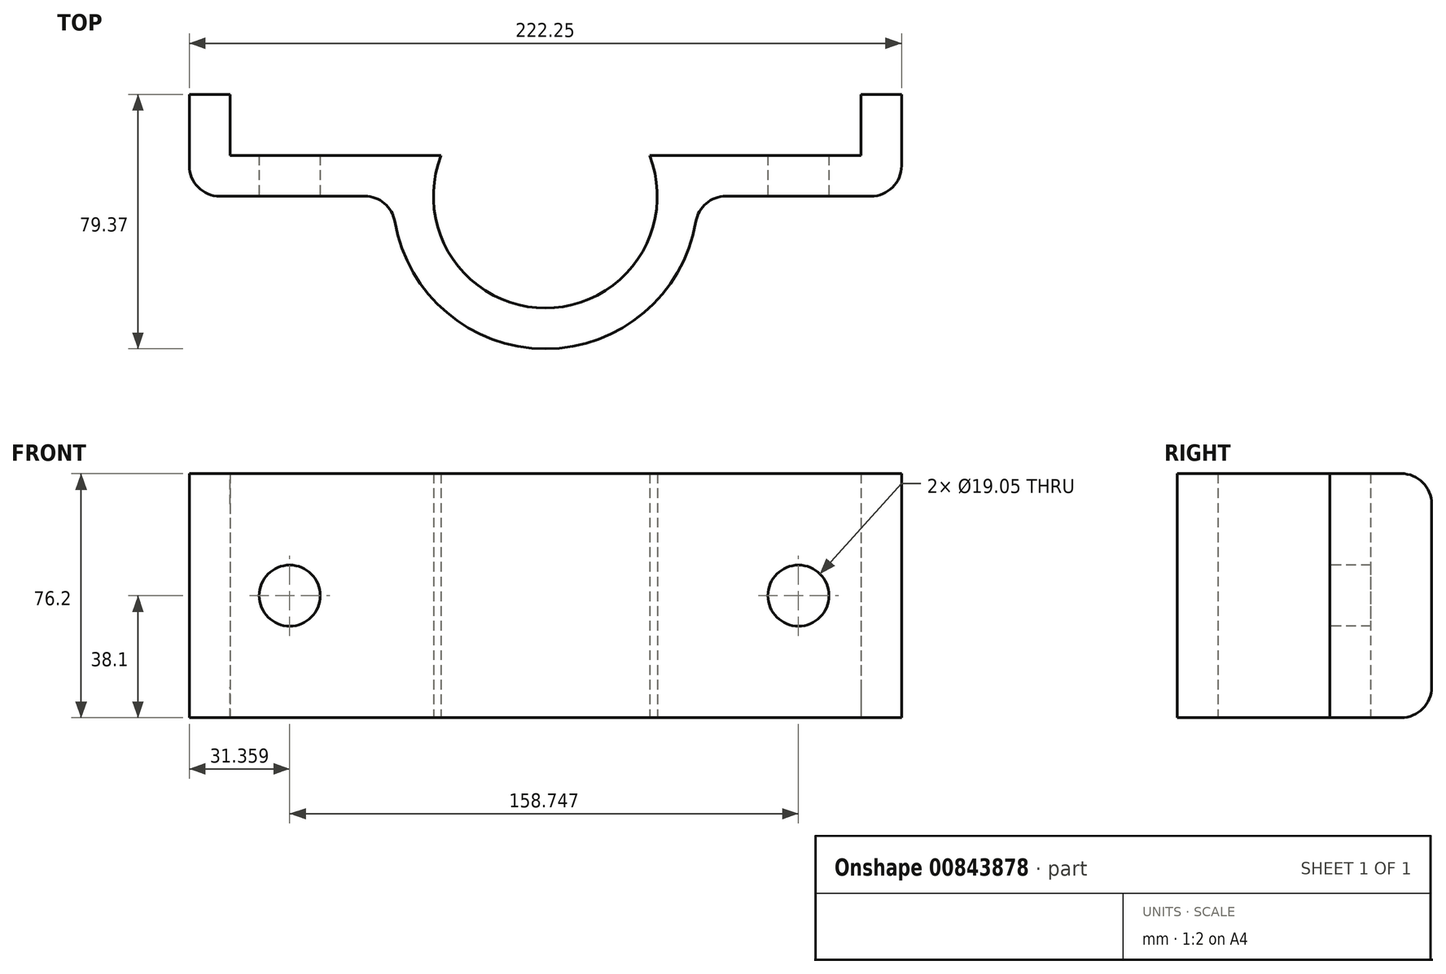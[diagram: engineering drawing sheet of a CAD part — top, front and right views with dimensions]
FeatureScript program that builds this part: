
annotation { "Feature Type Name" : "Feature", "Feature Type Description" : "" }
export const myFeature = defineFeature(function(context is Context, id is Id, definition is map)
    precondition{}
    {
        {
            var Q0;
            Q0=qCreatedBy(makeId("Top.planeOp"),FACE);
            var sketch = newSketch(context, id + "F0", { "sketchPlane" : qUnion([Q0])});
            skLineSegment(sketch, "E0", {"start": v(-41.29, 31.75) * mm, "end": v(-53.99, 31.75) * mm});
            skLineSegment(sketch, "E1", {"start": v(-53.99, 31.75) * mm, "end": v(-53.99, 9.52) * mm});
            skLineSegment(sketch, "E2", {"start": v(-41.29, 31.75) * mm, "end": v(-41.29, 12.7) * mm});
            skLineSegment(sketch, "E3", {"start": v(155.56, 31.75) * mm, "end": v(168.26, 31.75) * mm});
            skLineSegment(sketch, "E4", {"start": v(168.26, 31.75) * mm, "end": v(168.26, 9.53) * mm});
            skLineSegment(sketch, "E5", {"start": v(155.56, 12.7) * mm, "end": v(155.56, 31.75) * mm});
            skArc(sketch, "E6", {"start": v(24.6, 12.7) * mm, "mid": v(57.14, -34.93) * mm, "end": v(89.67, 12.7) * mm});
            skArc(sketch, "E7", {"start": v(10.18, -7.94) * mm, "mid": v(57.14, -47.62) * mm, "end": v(104.1, -7.94) * mm});
            skLineSegment(sketch, "E8", {"start": v(-41.29, 12.7) * mm, "end": v(24.6, 12.7) * mm});
            skLineSegment(sketch, "E9.trimOffspring", {"start": v(89.67, 12.7) * mm, "end": v(155.56, 12.7) * mm});
            skPoint(sketch, "E10.end.orphan", {"position": v(155.56, 0) * mm});
            skLineSegment(sketch, "E11", {"start": v(113.5, 0) * mm, "end": v(158.74, 0) * mm});
            skPoint(sketch, "E12.visualSharp", {"position": v(168.26, 0) * mm});
            skArc(sketch, "E12.filletArc", {"start": v(158.74, 0) * mm, "mid": v(165.47, 2.79) * mm, "end": v(168.26, 9.53) * mm});
            skPoint(sketch, "E13.visualSharp", {"position": v(104.76, 0) * mm});
            skArc(sketch, "E13.filletArc", {"start": v(113.5, 0) * mm, "mid": v(107.34, -2.25) * mm, "end": v(104.1, -7.94) * mm});
            skPoint(sketch, "E14.visualSharp", {"position": v(9.51, 0) * mm});
            skArc(sketch, "E14.filletArc", {"start": v(10.18, -7.94) * mm, "mid": v(6.94, -2.25) * mm, "end": v(0.79, 0) * mm});
            skPoint(sketch, "E15.end.orphan", {"position": v(-41.29, 0) * mm});
            skLineSegment(sketch, "E16", {"start": v(-44.46, 0) * mm, "end": v(0.79, 0) * mm});
            skPoint(sketch, "E17.visualSharp", {"position": v(-53.99, 0) * mm});
            skArc(sketch, "E17.filletArc", {"start": v(-53.99, 9.52) * mm, "mid": v(-51.2, 2.79) * mm, "end": v(-44.46, 0) * mm});
            skSolve(sketch);
        }
        {
            var Q0;
            Q0 = qSketchRegion(id + "F0", true);
            extrude(context, id + "F1", {"entities" : qUnion([Q0]), "depth" : 76.2 * mm, "offsetDistance" : 25.4 * mm});
        }
        {
            var Q0;
            Q0=makeQuery(id+"F1.opExtrude","SWEPT_FACE",FACE,{"disambiguationData":[OSD([sQuery(id+"F0.wireOp",EDGE,"E11")])]});
            var sketch = newSketch(context, id + "F2", { "sketchPlane" : qUnion([Q0])});
            skCircle(sketch, "E18", {"center": v(136.12, 38.1) * mm, "radius": 9.53 * mm});
            skPoint(sketch, "E19.orphan", {"position": v(136.12, 76.2) * mm});
            skPoint(sketch, "E20.start.orphan", {"position": v(136.12, 0) * mm});
            skCircle(sketch, "E21", {"center": v(-22.63, 38.1) * mm, "radius": 9.53 * mm});
            skSolve(sketch);
        }
        {
            var Q0;
            Q0 = qSketchRegion(id + "F2", true);
            extrude(context, id + "F3", {"entities" : qUnion([Q0]), "operationType" : NewBodyOperationType.REMOVE, "oppositeDirection" : true, "depth" : 25.4 * mm, "offsetDistance" : 25.4 * mm});
        }
        {
            var Q0;
            Q0=makeQuery(id+"F1.opExtrude","CAP_EDGE",EDGE,{"disambiguationData":[OSD([sQuery(id+"F0.wireOp",EDGE,"E0")])],"isStart":false});
            var Q1;
            Q1=makeQuery(id+"F1.opExtrude","CAP_EDGE",EDGE,{"disambiguationData":[OSD([sQuery(id+"F0.wireOp",EDGE,"E0")])],"isStart":true});
            var Q2;
            Q2=makeQuery(id+"F1.opExtrude","CAP_EDGE",EDGE,{"disambiguationData":[OSD([sQuery(id+"F0.wireOp",EDGE,"E3")])],"isStart":true});
            var Q3;
            Q3=makeQuery(id+"F1.opExtrude","CAP_EDGE",EDGE,{"disambiguationData":[OSD([sQuery(id+"F0.wireOp",EDGE,"E3")])],"isStart":false});
            fillet(context, id + "F4", {"entities" : qUnion([Q0, Q1, Q2, Q3]), "radius" : 9.52 * mm, "tangentPropagation" : true, "allowEdgeOverflow" : false});
        }
    });
